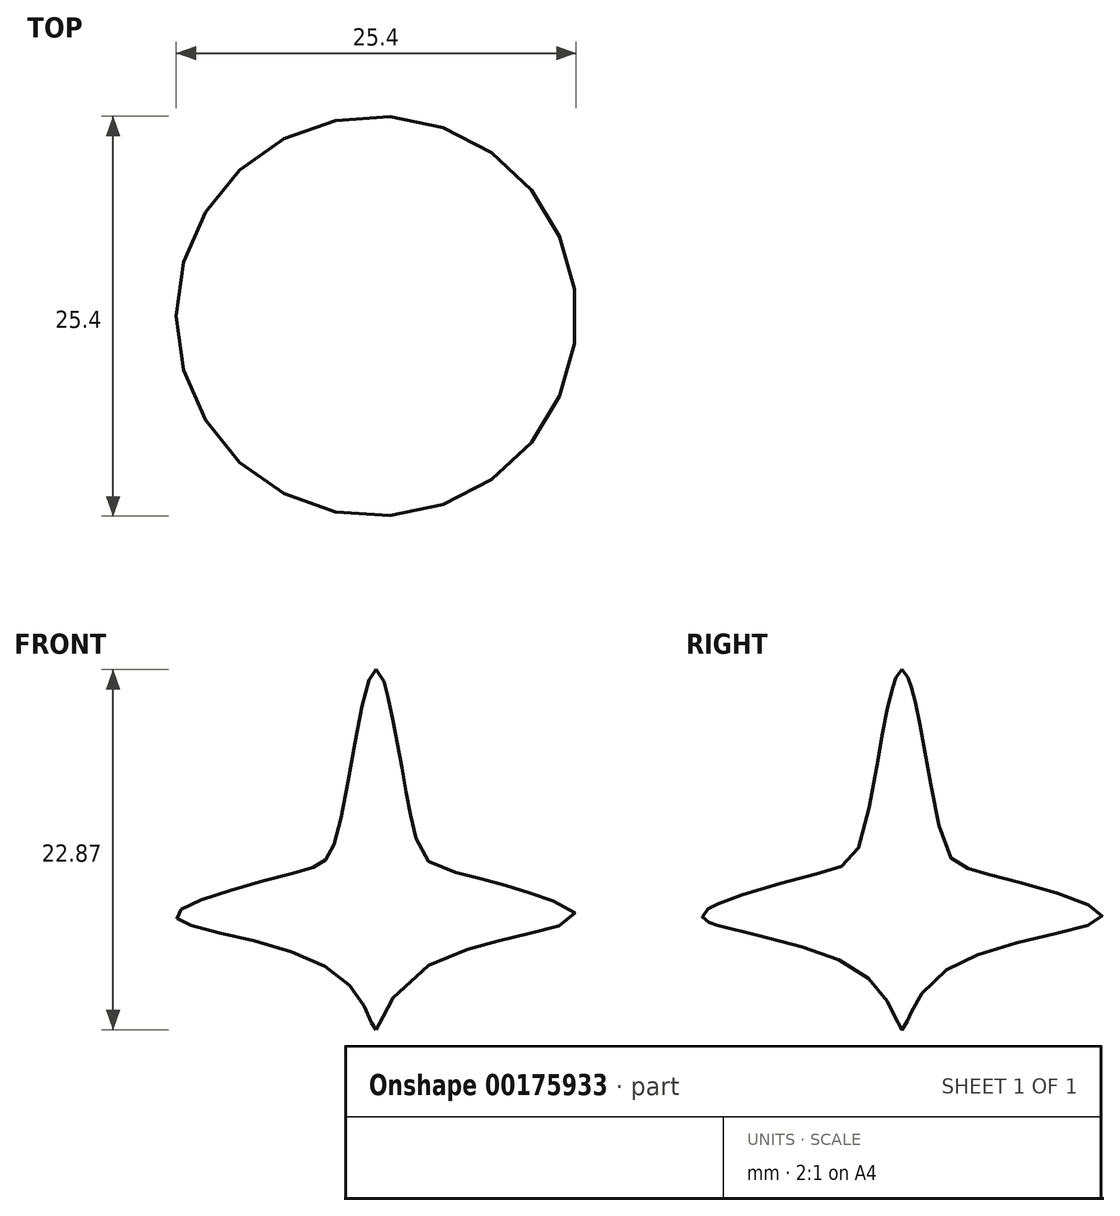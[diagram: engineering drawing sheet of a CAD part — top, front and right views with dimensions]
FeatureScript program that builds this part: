
annotation { "Feature Type Name" : "Feature", "Feature Type Description" : "" }
export const myFeature = defineFeature(function(context is Context, id is Id, definition is map)
    precondition{}
    {
        {
            var Q0;
            Q0=qCreatedBy(makeId("Front.planeOp"),FACE);
            var sketch = newSketch(context, id + "F0", { "sketchPlane" : qUnion([Q0])});
            skFitSpline(sketch, "E0", {"points": [v(0, 22.87) * mm, v(-2.54, 12.18) * mm, v(-5.08, 9.98) * mm, v(-12.7, 7.21) * mm, v(-2.54, 3.6) * mm, v(0, 0) * mm, v(2.54, 3.7) * mm, v(12.7, 7.21) * mm, v(5.08, 9.98) * mm, v(2.54, 12.18) * mm, v(0, 22.87) * mm]});
            skLineSegment(sketch, "E1", {"start": v(-12.7, 7.21) * mm, "end": v(12.7, 7.21) * mm, "construction": true});
            skLineSegment(sketch, "E2", {"start": v(-2.54, 12.18) * mm, "end": v(2.54, 12.18) * mm, "construction": true});
            skLineSegment(sketch, "E3", {"start": v(-5.08, 9.98) * mm, "end": v(5.08, 9.98) * mm, "construction": true});
            skPoint(sketch, "E4", {"position": v(0, 12.18) * mm});
            skPoint(sketch, "E5", {"position": v(0, 9.98) * mm});
            skPoint(sketch, "E6", {"position": v(0, 7.21) * mm});
            skLineSegment(sketch, "E7", {"start": v(-2.54, 3.6) * mm, "end": v(2.54, 3.7) * mm, "construction": true});
            skPoint(sketch, "E8", {"position": v(0, 3.64) * mm});
            skLineSegment(sketch, "E9", {"start": v(0, 28.2) * mm, "end": v(0, -20.68) * mm});
            skSolve(sketch);
        }
        {
            var Q0;
            {var subQ0=sQuery(id+"F0.wireOp",EDGE,"E9");var subQ1=sQuery(id+"F0.wireOp",EDGE,"E0");var subQ2=makeQuery(id+"F0.imprint","INTERSECT",VERTEX,{"disambiguationData":[OD(0.0)],"derivedFrom":[subQ1,subQ0]});Q0=makeQuery(id+"F0.imprint","IMPRINT",FACE,{"disambiguationData":[TD([[makeQuery(id+"F0.imprint","IMPRINT",EDGE,{"disambiguationData":[TD([[subQ2,1.0]])],"derivedFrom":subQ1}),1.0]])]});}
            var Q1;
            Q1=sQuery(id+"F0.wireOp",EDGE,"E9");
            revolve(context, id + "F1", {"entities" : qUnion([Q0]), "axis" : qUnion([Q1]), "revolveType" : RevolveType.FULL});
        }
    });
